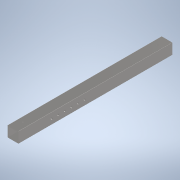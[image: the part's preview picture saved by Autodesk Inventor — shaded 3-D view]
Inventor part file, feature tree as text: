
AUTODESK INVENTOR PART (.ipt)
format: ipt  version: 2021 (Build 250183000, 183)  size: 185,856 bytes
history: native  units: mm
features: sketch x3, hole x2, extrude x1, fillet x1
ambient origin geometry x8: Origin, YZ Plane, XZ Plane, XY Plane, X Axis, Y Axis, Z Axis, Center Point
bodies: Solid1 (feature_tree)
feature tree (7):
  extrude  "Extrusion1"  Depth=50.0mm
  fillet  "Fillet1"  Radius=25.0mm
  hole  "endHoles"  [1 undecoded]
  hole  "Hole4"  [1 undecoded]
  sketch  "Sketch1"  dims[d0=50.0mm d1=50.0mm d2=25.0mm]
  sketch  "Sketch2"  dims[d3=25.0mm d4=5.0mm]
  sketch  "Sketch3"  dims[d5=700.0mm d6=0.0mm d7=2.0mm d8=45.0mm d9=0.0mm d10=45.0mm d11=0.0mm d12=10.0mm d13=6.0mm d14=4.0mm d15=2.0mm d16=90.0deg d17=8.0mm d18=0.0mm d19=400.0mm d21=0.0mm d22=0.0mm d42=10.0mm d43=6.0mm d44=4.0mm d45=2.0mm d46=90.0deg d47=8.0mm d48=20.594885mm d49=150.0mm]
note: 2 required parameter values undecoded (feature->parameter linkage not recoverable at this tier; creation-order binding heuristic only, values carry confidence <= 0.55)
